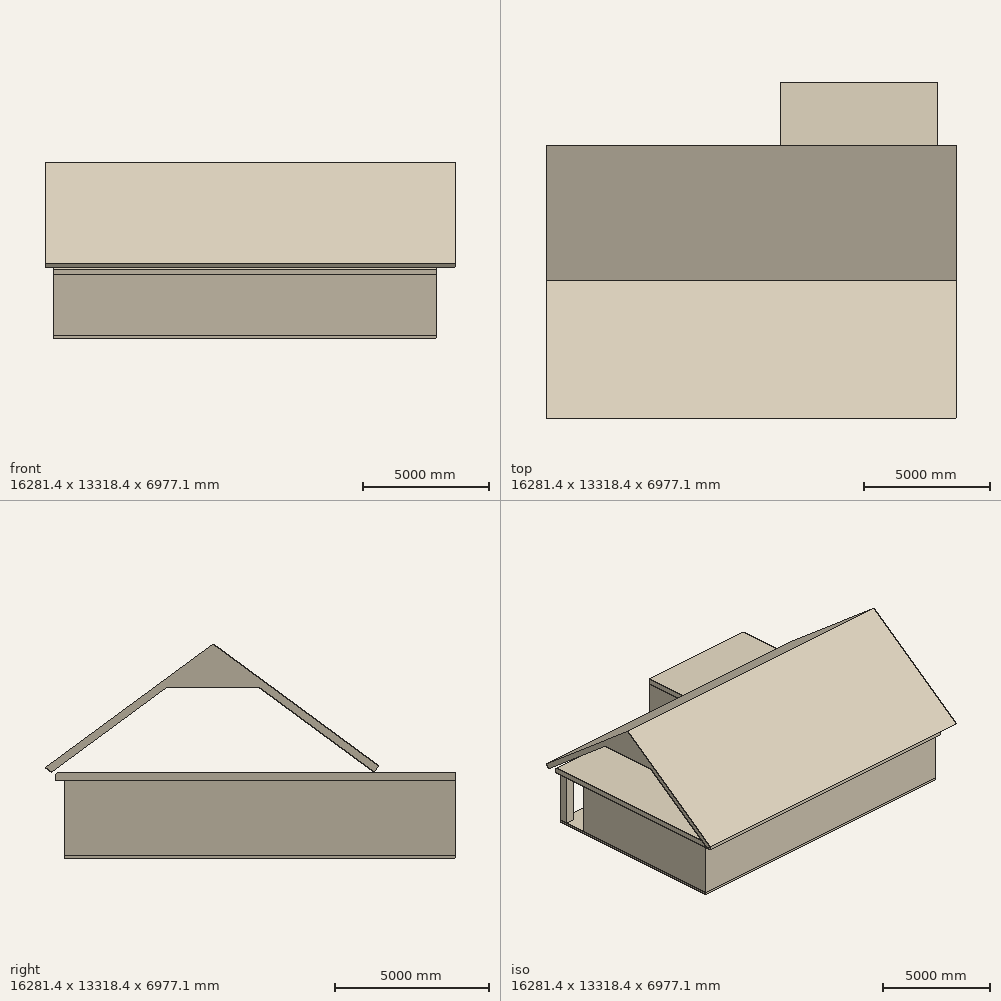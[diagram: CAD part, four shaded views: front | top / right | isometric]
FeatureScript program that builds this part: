
annotation { "Feature Type Name" : "Feature", "Feature Type Description" : "" }
export const myFeature = defineFeature(function(context is Context, id is Id, definition is map)
    precondition{}
    {
        {
            var Q0;
            Q0=qCreatedBy(makeId("Top.planeOp"),FACE);
            var sketch = newSketch(context, id + "F0", { "sketchPlane" : qUnion([Q0])});
            skLineSegment(sketch, "E0", {"start": v(0, 0) * mm, "end": v(0, 7721.6) * mm});
            skLineSegment(sketch, "E1", {"start": v(0, 7721.6) * mm, "end": v(5632.45, 7721.6) * mm});
            skLineSegment(sketch, "E2", {"start": v(5632.45, 7721.6) * mm, "end": v(5632.45, 9245.6) * mm});
            skLineSegment(sketch, "E3", {"start": v(5632.45, 9245.6) * mm, "end": v(8953.5, 9245.6) * mm});
            skLineSegment(sketch, "E4", {"start": v(8953.5, 9245.6) * mm, "end": v(8953.5, 12293.6) * mm});
            skLineSegment(sketch, "E5", {"start": v(8953.5, 12293.6) * mm, "end": v(14782.8, 12293.6) * mm});
            skLineSegment(sketch, "E6", {"start": v(14782.8, 12293.6) * mm, "end": v(14782.8, 0) * mm});
            skLineSegment(sketch, "E7", {"start": v(14782.8, 0) * mm, "end": v(0, 0) * mm});
            skLineSegment(sketch, "E8.0", {"start": v(5429.25, 7924.8) * mm, "end": v(5429.25, 9448.8) * mm});
            skLineSegment(sketch, "E8.1", {"start": v(-203.2, 7924.8) * mm, "end": v(5429.25, 7924.8) * mm});
            skLineSegment(sketch, "E8.2", {"start": v(5429.25, 9448.8) * mm, "end": v(8750.3, 9448.8) * mm});
            skLineSegment(sketch, "E8.3", {"start": v(-203.2, -203.2) * mm, "end": v(-203.2, 7924.8) * mm});
            skLineSegment(sketch, "E8.4", {"start": v(8750.3, 9448.8) * mm, "end": v(8750.3, 12496.8) * mm});
            skLineSegment(sketch, "E8.5", {"start": v(8750.3, 12496.8) * mm, "end": v(14986, 12496.8) * mm});
            skLineSegment(sketch, "E8.6", {"start": v(14986, 12496.8) * mm, "end": v(14986, -203.2) * mm});
            skLineSegment(sketch, "E8.7", {"start": v(14986, -203.2) * mm, "end": v(-203.2, -203.2) * mm});
            skLineSegment(sketch, "E9.bottom", {"start": v(-203.2, 9448.8) * mm, "end": v(254, 9448.8) * mm});
            skLineSegment(sketch, "E9.top", {"start": v(-203.2, 8991.6) * mm, "end": v(254, 8991.6) * mm});
            skLineSegment(sketch, "E9.left", {"start": v(-203.2, 9448.8) * mm, "end": v(-203.2, 8991.6) * mm});
            skLineSegment(sketch, "E9.right", {"start": v(254, 9448.8) * mm, "end": v(254, 8991.6) * mm});
            skLineSegment(sketch, "E10.bottom", {"start": v(3448.05, 9448.8) * mm, "end": v(3905.25, 9448.8) * mm});
            skLineSegment(sketch, "E10.top", {"start": v(3448.05, 8991.6) * mm, "end": v(3905.25, 8991.6) * mm});
            skLineSegment(sketch, "E10.left", {"start": v(3448.05, 9448.8) * mm, "end": v(3448.05, 8991.6) * mm});
            skLineSegment(sketch, "E10.right", {"start": v(3905.25, 9448.8) * mm, "end": v(3905.25, 8991.6) * mm});
            skSolve(sketch);
        }
        {
            var Q0;
            Q0 = qSketchRegion(id + "F0", true);
            var Q1;
            Q1=sQuery(id+"F0.wireOp",EDGE,"E8.3");
            extrude(context, id + "F1", {"entities" : qUnion([Q0]), "surfaceEntities" : qUnion([Q1]), "depth" : 2438.4 * mm});
        }
        {
            var Q0;
            Q0=qCreatedBy(makeId("Top.planeOp"),FACE);
            var sketch = newSketch(context, id + "F2", { "sketchPlane" : qUnion([Q0])});
            skLineSegment(sketch, "E11.bottom", {"start": v(3441.7, 7721.6) * mm, "end": v(3327.4, 7721.6) * mm});
            skLineSegment(sketch, "E11.top", {"start": v(3441.7, 0) * mm, "end": v(3327.4, 0) * mm});
            skLineSegment(sketch, "E11.left", {"start": v(3441.7, 7721.6) * mm, "end": v(3441.7, 0) * mm});
            skLineSegment(sketch, "E11.right", {"start": v(3327.4, 7721.6) * mm, "end": v(3327.4, 0) * mm});
            skLineSegment(sketch, "E12.bottom", {"start": v(8953.5, 9245.6) * mm, "end": v(8839.2, 9245.6) * mm});
            skLineSegment(sketch, "E12.top", {"start": v(8953.5, 4267.2) * mm, "end": v(8839.2, 4267.2) * mm});
            skLineSegment(sketch, "E12.left", {"start": v(8953.5, 9245.6) * mm, "end": v(8953.5, 4267.2) * mm});
            skLineSegment(sketch, "E12.right", {"start": v(8839.2, 9245.6) * mm, "end": v(8839.2, 4267.2) * mm});
            skLineSegment(sketch, "E13.bottom", {"start": v(8953.5, 4267.2) * mm, "end": v(14782.8, 4267.2) * mm});
            skLineSegment(sketch, "E13.top", {"start": v(8953.5, 4381.5) * mm, "end": v(14782.8, 4381.5) * mm});
            skLineSegment(sketch, "E13.left", {"start": v(8953.5, 4267.2) * mm, "end": v(8953.5, 4381.5) * mm});
            skLineSegment(sketch, "E13.right", {"start": v(14782.8, 4267.2) * mm, "end": v(14782.8, 4381.5) * mm});
            skLineSegment(sketch, "E14.bottom", {"start": v(8953.5, 5651.5) * mm, "end": v(14782.8, 5651.5) * mm});
            skLineSegment(sketch, "E14.top", {"start": v(8953.5, 5765.8) * mm, "end": v(14782.8, 5765.8) * mm});
            skLineSegment(sketch, "E14.left", {"start": v(8953.5, 5651.5) * mm, "end": v(8953.5, 5765.8) * mm});
            skLineSegment(sketch, "E14.right", {"start": v(14782.8, 5651.5) * mm, "end": v(14782.8, 5765.8) * mm});
            skLineSegment(sketch, "E15.bottom", {"start": v(12230.1, 5651.5) * mm, "end": v(12344.4, 5651.5) * mm});
            skLineSegment(sketch, "E15.top", {"start": v(12230.1, 4381.5) * mm, "end": v(12344.4, 4381.5) * mm});
            skLineSegment(sketch, "E15.left", {"start": v(12230.1, 5651.5) * mm, "end": v(12230.1, 4381.5) * mm});
            skLineSegment(sketch, "E15.right", {"start": v(12344.4, 5651.5) * mm, "end": v(12344.4, 4381.5) * mm});
            skLineSegment(sketch, "E16.bottom", {"start": v(3327.4, 3162.3) * mm, "end": v(0, 3162.3) * mm});
            skLineSegment(sketch, "E16.top", {"start": v(3327.4, 3048) * mm, "end": v(0, 3048) * mm});
            skLineSegment(sketch, "E16.left", {"start": v(3327.4, 3162.3) * mm, "end": v(3327.4, 3048) * mm});
            skLineSegment(sketch, "E16.right", {"start": v(0, 3162.3) * mm, "end": v(0, 3048) * mm});
            skLineSegment(sketch, "E17", {"start": v(0, 1638.3) * mm, "end": v(0, 1524) * mm});
            skLineSegment(sketch, "E18", {"start": v(0, 1524) * mm, "end": v(1689.1, 1524) * mm});
            skLineSegment(sketch, "E19", {"start": v(1689.1, 1524) * mm, "end": v(1689.1, 0) * mm});
            skLineSegment(sketch, "E20", {"start": v(1689.1, 0) * mm, "end": v(1803.4, 0) * mm});
            skLineSegment(sketch, "E21.0", {"start": v(1803.4, 1638.3) * mm, "end": v(1803.4, 0) * mm});
            skLineSegment(sketch, "E21.2", {"start": v(0, 1638.3) * mm, "end": v(1803.4, 1638.3) * mm});
            skLineSegment(sketch, "E22.bottom", {"start": v(4381.5, 6553.2) * mm, "end": v(4546.6, 6553.2) * mm});
            skLineSegment(sketch, "E22.top", {"start": v(4381.5, 3048) * mm, "end": v(4546.6, 3048) * mm});
            skLineSegment(sketch, "E22.left", {"start": v(4381.5, 6553.2) * mm, "end": v(4381.5, 3048) * mm});
            skLineSegment(sketch, "E22.right", {"start": v(4546.6, 6553.2) * mm, "end": v(4546.6, 3048) * mm});
            skLineSegment(sketch, "E23.bottom", {"start": v(4381.5, 3048) * mm, "end": v(3441.7, 3048) * mm});
            skLineSegment(sketch, "E23.top", {"start": v(4381.5, 3162.3) * mm, "end": v(3441.7, 3162.3) * mm});
            skLineSegment(sketch, "E23.left", {"start": v(4381.5, 3048) * mm, "end": v(4381.5, 3162.3) * mm});
            skLineSegment(sketch, "E23.right", {"start": v(3441.7, 3048) * mm, "end": v(3441.7, 3162.3) * mm});
            skLineSegment(sketch, "E24.bottom", {"start": v(4381.5, 4495.8) * mm, "end": v(3441.7, 4495.8) * mm});
            skLineSegment(sketch, "E24.top", {"start": v(4381.5, 4610.1) * mm, "end": v(3441.7, 4610.1) * mm});
            skLineSegment(sketch, "E24.left", {"start": v(4381.5, 4495.8) * mm, "end": v(4381.5, 4610.1) * mm});
            skLineSegment(sketch, "E24.right", {"start": v(3441.7, 4495.8) * mm, "end": v(3441.7, 4610.1) * mm});
            skLineSegment(sketch, "E25.bottom", {"start": v(2717.8, 723.9) * mm, "end": v(3327.4, 723.9) * mm});
            skLineSegment(sketch, "E25.top", {"start": v(2717.8, 609.6) * mm, "end": v(3327.4, 609.6) * mm});
            skLineSegment(sketch, "E25.left", {"start": v(2717.8, 723.9) * mm, "end": v(2717.8, 609.6) * mm});
            skLineSegment(sketch, "E25.right", {"start": v(3327.4, 723.9) * mm, "end": v(3327.4, 609.6) * mm});
            skLineSegment(sketch, "E26.bottom", {"start": v(1689.1, 3048) * mm, "end": v(1803.4, 3048) * mm});
            skLineSegment(sketch, "E26.top", {"start": v(1689.1, 2495.55) * mm, "end": v(1803.4, 2495.55) * mm});
            skLineSegment(sketch, "E26.left", {"start": v(1689.1, 3048) * mm, "end": v(1689.1, 2495.55) * mm});
            skLineSegment(sketch, "E26.right", {"start": v(1803.4, 3048) * mm, "end": v(1803.4, 2495.55) * mm});
            skLineSegment(sketch, "E27.bottom", {"start": v(1803.4, 1943.1) * mm, "end": v(1689.1, 1943.1) * mm});
            skLineSegment(sketch, "E27.top", {"start": v(1803.4, 1638.3) * mm, "end": v(1689.1, 1638.3) * mm});
            skLineSegment(sketch, "E27.left", {"start": v(1803.4, 1943.1) * mm, "end": v(1803.4, 1638.3) * mm});
            skLineSegment(sketch, "E27.right", {"start": v(1689.1, 1943.1) * mm, "end": v(1689.1, 1638.3) * mm});
            skLineSegment(sketch, "E28.bottom", {"start": v(1803.4, 723.9) * mm, "end": v(2108.2, 723.9) * mm});
            skLineSegment(sketch, "E28.top", {"start": v(1803.4, 609.6) * mm, "end": v(2108.2, 609.6) * mm});
            skLineSegment(sketch, "E28.left", {"start": v(1803.4, 723.9) * mm, "end": v(1803.4, 609.6) * mm});
            skLineSegment(sketch, "E28.right", {"start": v(2108.2, 723.9) * mm, "end": v(2108.2, 609.6) * mm});
            skLineSegment(sketch, "E29", {"start": v(1689.1, 2495.55) * mm, "end": v(1689.1, 1943.1) * mm, "construction": true});
            skSolve(sketch);
        }
        {
            var Q0;
            Q0 = qSketchRegion(id + "F2", true);
            extrude(context, id + "F3", {"entities" : qUnion([Q0]), "operationType" : NewBodyOperationType.ADD, "depth" : 2438.4 * mm});
        }
        {
            var Q0;
            {var subQ0=sQuery(id+"F2.wireOp",EDGE,"E11.left");Q0=makeQuery(id+"F3.opExtrude","SWEPT_FACE",FACE,{"disambiguationData":[OSD([subQ0]),TDD([makeQuery(id+"F2.imprint","IMPRINT",EDGE,{"disambiguationData":[TD([[makeQuery(id+"F2.imprint","INTERSECT",VERTEX,{"derivedFrom":[sQuery(id+"F2.wireOp",EDGE,"E11.bottom"),subQ0]}),-1.0]])],"derivedFrom":subQ0})])]});}
            var sketch = newSketch(context, id + "F4", { "sketchPlane" : qUnion([Q0])});
            skLineSegment(sketch, "E30", {"start": v(6540.5, 0) * mm, "end": v(6540.5, 195.94) * mm});
            skLineSegment(sketch, "E31", {"start": v(6540.5, 195.94) * mm, "end": v(6280.64, 195.94) * mm});
            skLineSegment(sketch, "E32", {"start": v(6280.64, 195.94) * mm, "end": v(6280.64, 391.89) * mm});
            skLineSegment(sketch, "E33", {"start": v(6280.64, 391.89) * mm, "end": v(6020.78, 391.89) * mm});
            skLineSegment(sketch, "E34", {"start": v(6020.78, 391.89) * mm, "end": v(6020.78, 587.83) * mm});
            skLineSegment(sketch, "E35", {"start": v(6020.78, 587.83) * mm, "end": v(5760.92, 587.83) * mm});
            skLineSegment(sketch, "E36", {"start": v(5760.92, 587.83) * mm, "end": v(5760.92, 783.77) * mm});
            skLineSegment(sketch, "E37", {"start": v(5760.92, 783.77) * mm, "end": v(5501.05, 783.77) * mm});
            skLineSegment(sketch, "E38", {"start": v(5501.05, 783.77) * mm, "end": v(5501.05, 979.71) * mm});
            skLineSegment(sketch, "E39", {"start": v(5501.05, 979.71) * mm, "end": v(5241.2, 979.71) * mm});
            skLineSegment(sketch, "E40", {"start": v(5241.2, 979.71) * mm, "end": v(5241.2, 1175.66) * mm});
            skLineSegment(sketch, "E41", {"start": v(5241.2, 1175.66) * mm, "end": v(4981.33, 1175.66) * mm});
            skLineSegment(sketch, "E42", {"start": v(4981.33, 1175.66) * mm, "end": v(4981.33, 1371.6) * mm});
            skLineSegment(sketch, "E43", {"start": v(4981.33, 1371.6) * mm, "end": v(4721.47, 1371.6) * mm});
            skLineSegment(sketch, "E44", {"start": v(4721.47, 1371.6) * mm, "end": v(4721.47, 1567.54) * mm});
            skLineSegment(sketch, "E45", {"start": v(4721.47, 1567.54) * mm, "end": v(4461.6, 1567.54) * mm});
            skLineSegment(sketch, "E46", {"start": v(4461.6, 1567.54) * mm, "end": v(4461.6, 1763.49) * mm});
            skLineSegment(sketch, "E47", {"start": v(4461.6, 1763.49) * mm, "end": v(4201.75, 1763.49) * mm});
            skLineSegment(sketch, "E48", {"start": v(4201.75, 1763.49) * mm, "end": v(4201.75, 1959.43) * mm});
            skLineSegment(sketch, "E49", {"start": v(4201.75, 1959.43) * mm, "end": v(3941.88, 1959.43) * mm});
            skLineSegment(sketch, "E50", {"start": v(3941.88, 1959.43) * mm, "end": v(3941.88, 2155.37) * mm});
            skLineSegment(sketch, "E51", {"start": v(3941.88, 2155.37) * mm, "end": v(3682.02, 2155.37) * mm});
            skLineSegment(sketch, "E52", {"start": v(3682.02, 2155.37) * mm, "end": v(3682.02, 2351.31) * mm});
            skLineSegment(sketch, "E53", {"start": v(3682.02, 2351.31) * mm, "end": v(3422.16, 2351.31) * mm});
            skLineSegment(sketch, "E54", {"start": v(3422.16, 2351.31) * mm, "end": v(3422.16, 2547.26) * mm});
            skLineSegment(sketch, "E55", {"start": v(3422.16, 2547.26) * mm, "end": v(3162.3, 2547.26) * mm});
            skLineSegment(sketch, "E56", {"start": v(3162.3, 2547.26) * mm, "end": v(3162.3, 2743.2) * mm, "construction": true});
            skLineSegment(sketch, "E57", {"start": v(3162.3, 2547.26) * mm, "end": v(3162.3, 2184.4) * mm});
            skLineSegment(sketch, "E58", {"start": v(3162.3, 2184.4) * mm, "end": v(3559.15, 2184.4) * mm});
            skLineSegment(sketch, "E59", {"start": v(3559.15, 2184.4) * mm, "end": v(6456.12, 0) * mm});
            skLineSegment(sketch, "E60", {"start": v(6456.12, 0) * mm, "end": v(6540.5, 0) * mm});
            skLineSegment(sketch, "E61", {"start": v(3162.3, 2547.26) * mm, "end": v(6540.5, 0) * mm, "construction": true});
            skSolve(sketch);
        }
        {
            var Q0;
            Q0=makeQuery(id+"F3.opExtrude","SWEPT_FACE",FACE,{"disambiguationData":[OSD([sQuery(id+"F2.wireOp",EDGE,"E22.right")])]});
            var sketch = newSketch(context, id + "F5", { "sketchPlane" : qUnion([Q0])});
            skLineSegment(sketch, "E62", {"start": v(4902.6, 2438.4) * mm, "end": v(6553.2, 1193.8) * mm});
            skLineSegment(sketch, "E63", {"start": v(6553.2, 1193.8) * mm, "end": v(6553.2, 2438.4) * mm});
            skLineSegment(sketch, "E64", {"start": v(6553.2, 2438.4) * mm, "end": v(4902.6, 2438.4) * mm});
            skSolve(sketch);
        }
        {
            var Q0;
            Q0 = qSketchRegion(id + "F5", true);
            extrude(context, id + "F6", {"entities" : qUnion([Q0]), "operationType" : NewBodyOperationType.REMOVE, "endBound" : BoundingType.UP_TO_NEXT, "oppositeDirection" : true, "depth" : 25.4 * mm});
        }
        {
            var Q0;
            {var subQ0=sQuery(id+"F2.wireOp",EDGE,"E11.left");Q0=makeQuery(id+"F3.opExtrude","SWEPT_FACE",FACE,{"disambiguationData":[OSD([subQ0]),TDD([makeQuery(id+"F2.imprint","IMPRINT",EDGE,{"disambiguationData":[TD([[makeQuery(id+"F2.imprint","INTERSECT",VERTEX,{"derivedFrom":[subQ0,sQuery(id+"F2.wireOp",EDGE,"E23.top"),sQuery(id+"F2.wireOp",EDGE,"E23.right")]}),1.0]])],"derivedFrom":subQ0})])]});}
            var sketch = newSketch(context, id + "F7", { "sketchPlane" : qUnion([Q0])});
            skLineSegment(sketch, "E65", {"start": v(4495.8, 2438.4) * mm, "end": v(4610.1, 2438.4) * mm});
            skLineSegment(sketch, "E66", {"start": v(4610.1, 2438.4) * mm, "end": v(4610.1, 1391.95) * mm});
            skLineSegment(sketch, "E67", {"start": v(4610.1, 1391.95) * mm, "end": v(4495.8, 1478.14) * mm});
            skLineSegment(sketch, "E68", {"start": v(4495.8, 1478.14) * mm, "end": v(4495.8, 2438.4) * mm});
            skSolve(sketch);
        }
        {
            var Q0;
            Q0 = qSketchRegion(id + "F7", true);
            var Q1;
            {var subQ0=sQuery(id+"F2.wireOp",EDGE,"E22.left");Q1=makeQuery(id+"F3.opExtrude","SWEPT_FACE",FACE,{"disambiguationData":[OSD([subQ0]),TDD([makeQuery(id+"F2.imprint","IMPRINT",EDGE,{"disambiguationData":[TD([[makeQuery(id+"F2.imprint","INTERSECT",VERTEX,{"derivedFrom":[subQ0,sQuery(id+"F2.wireOp",EDGE,"E23.top"),sQuery(id+"F2.wireOp",EDGE,"E23.left")]}),1.0]])],"derivedFrom":subQ0})])]});}
            extrude(context, id + "F8", {"entities" : qUnion([Q0]), "operationType" : NewBodyOperationType.REMOVE, "endBound" : BoundingType.UP_TO_SURFACE, "endBoundEntityFace" : qUnion([Q1]), "depth" : 25.4 * mm});
        }
        {
            var Q0;
            Q0 = qSketchRegion(id + "F4", true);
            var Q1;
            {var subQ0=sQuery(id+"F2.wireOp",EDGE,"E22.left");Q1=makeQuery(id+"F3.opExtrude","SWEPT_FACE",FACE,{"disambiguationData":[OSD([subQ0]),TDD([makeQuery(id+"F2.imprint","IMPRINT",EDGE,{"disambiguationData":[TD([[makeQuery(id+"F2.imprint","INTERSECT",VERTEX,{"derivedFrom":[subQ0,sQuery(id+"F2.wireOp",EDGE,"E23.top"),sQuery(id+"F2.wireOp",EDGE,"E23.left")]}),1.0]])],"derivedFrom":subQ0})])]});}
            var Q2;
            {var subQ0=sQuery(id+"F2.wireOp",EDGE,"E22.left");Q2=makeQuery(id+"F3.opExtrude","SWEPT_FACE",FACE,{"disambiguationData":[OSD([subQ0]),TDD([makeQuery(id+"F2.imprint","IMPRINT",EDGE,{"disambiguationData":[TD([[makeQuery(id+"F2.imprint","INTERSECT",VERTEX,{"derivedFrom":[subQ0,sQuery(id+"F2.wireOp",EDGE,"E23.top"),sQuery(id+"F2.wireOp",EDGE,"E23.left")]}),1.0]])],"derivedFrom":subQ0})])]});}
            extrude(context, id + "F9", {"entities" : qUnion([Q0]), "operationType" : NewBodyOperationType.ADD, "endBound" : BoundingType.UP_TO_SURFACE, "endBoundEntityFace" : qUnion([Q1]), "depth" : 660.4 * mm});
        }
        {
            var Q0;
            {var subQ0=sQuery(id+"F2.wireOp",EDGE,"E23.top");var subQ20=sQuery(id+"F2.wireOp",EDGE,"E11.left");var subQ22=sQuery(id+"F2.wireOp",EDGE,"E11.bottom");var subQ23=sQuery(id+"F0.wireOp",EDGE,"E1");Q0=makeQuery(id+"F9.boolean.opBoolean","SPLIT",FACE,{"disambiguationData":[TD([makeQuery(id+"F1.opExtrude","SWEPT_FACE",FACE,{"disambiguationData":[OSD([subQ23])]})])],"derivedFrom":makeQuery(id+"F8.boolean.opBoolean","MERGE",FACE,{"derivedFrom":[makeQuery(id+"F3.opExtrude","SWEPT_FACE",FACE,{"disambiguationData":[OSD([subQ20]),TDD([makeQuery(id+"F2.imprint","IMPRINT",EDGE,{"disambiguationData":[TD([[makeQuery(id+"F2.imprint","INTERSECT",VERTEX,{"derivedFrom":[subQ22,subQ20]}),-1.0]])],"derivedFrom":subQ20})])]}),makeQuery(id+"F3.opExtrude","SWEPT_FACE",FACE,{"disambiguationData":[OSD([subQ20]),TDD([makeQuery(id+"F2.imprint","IMPRINT",EDGE,{"disambiguationData":[TD([[makeQuery(id+"F2.imprint","INTERSECT",VERTEX,{"derivedFrom":[subQ20,subQ0,sQuery(id+"F2.wireOp",EDGE,"E23.right")]}),1.0]])],"derivedFrom":subQ20})])]}),makeQuery(id+"F8.opExtrude","CAP_FACE",FACE,{"disambiguationData":[OSD([sQuery(id+"F7.wireOp",EDGE,"E65"),sQuery(id+"F7.wireOp",EDGE,"E66"),sQuery(id+"F7.wireOp",EDGE,"E67"),sQuery(id+"F7.wireOp",EDGE,"E68")])],"isStart":true})]})});}
            var sketch = newSketch(context, id + "F10", { "sketchPlane" : qUnion([Q0])});
            skLineSegment(sketch, "E69.bottom", {"start": v(6724.65, 0) * mm, "end": v(7537.45, 0) * mm});
            skLineSegment(sketch, "E69.top", {"start": v(6724.65, 2032) * mm, "end": v(7537.45, 2032) * mm});
            skLineSegment(sketch, "E69.left", {"start": v(6724.65, 0) * mm, "end": v(6724.65, 2032) * mm});
            skLineSegment(sketch, "E69.right", {"start": v(7537.45, 0) * mm, "end": v(7537.45, 2032) * mm});
            skLineSegment(sketch, "E70", {"start": v(6724.65, 0) * mm, "end": v(6540.5, 0) * mm, "construction": true});
            skLineSegment(sketch, "E71", {"start": v(7537.45, 0) * mm, "end": v(7721.6, 0) * mm});
            skSolve(sketch);
        }
        {
            var Q0;
            Q0 = qSketchRegion(id + "F10", true);
            extrude(context, id + "F11", {"entities" : qUnion([Q0]), "operationType" : NewBodyOperationType.REMOVE, "endBound" : BoundingType.UP_TO_NEXT, "oppositeDirection" : true, "depth" : 25.4 * mm});
        }
        {
            var Q0;
            Q0=makeQuery(id+"F3.opExtrude","SWEPT_FACE",FACE,{"disambiguationData":[OSD([sQuery(id+"F2.wireOp",EDGE,"E19")])]});
            var sketch = newSketch(context, id + "F12", { "sketchPlane" : qUnion([Q0])});
            skLineSegment(sketch, "E72.bottom", {"start": v(-1422.4, 0) * mm, "end": v(-812.8, 0) * mm});
            skLineSegment(sketch, "E72.top", {"start": v(-1422.4, 2032) * mm, "end": v(-812.8, 2032) * mm});
            skLineSegment(sketch, "E72.left", {"start": v(-1422.4, 0) * mm, "end": v(-1422.4, 2032) * mm});
            skLineSegment(sketch, "E72.right", {"start": v(-812.8, 0) * mm, "end": v(-812.8, 2032) * mm});
            skSolve(sketch);
        }
        {
            var Q0;
            Q0 = qSketchRegion(id + "F12", true);
            extrude(context, id + "F13", {"entities" : qUnion([Q0]), "operationType" : NewBodyOperationType.REMOVE, "endBound" : BoundingType.UP_TO_NEXT, "oppositeDirection" : true, "depth" : 25.4 * mm});
        }
        {
            var Q0;
            Q0=makeQuery(id+"F3.opExtrude","SWEPT_FACE",FACE,{"disambiguationData":[OSD([sQuery(id+"F2.wireOp",EDGE,"E16.top")])]});
            var sketch = newSketch(context, id + "F14", { "sketchPlane" : qUnion([Q0])});
            skLineSegment(sketch, "E73.bottom", {"start": v(1955.8, 0) * mm, "end": v(2565.4, 0) * mm});
            skLineSegment(sketch, "E73.top", {"start": v(1955.8, 2032) * mm, "end": v(2565.4, 2032) * mm});
            skLineSegment(sketch, "E73.left", {"start": v(1955.8, 0) * mm, "end": v(1955.8, 2032) * mm});
            skLineSegment(sketch, "E73.right", {"start": v(2565.4, 0) * mm, "end": v(2565.4, 2032) * mm});
            skSolve(sketch);
        }
        {
            var Q0;
            Q0 = qSketchRegion(id + "F14", true);
            extrude(context, id + "F15", {"entities" : qUnion([Q0]), "operationType" : NewBodyOperationType.REMOVE, "endBound" : BoundingType.UP_TO_NEXT, "oppositeDirection" : true, "depth" : 25.4 * mm});
        }
        {
            var Q0;
            Q0=qCreatedBy(makeId("Top.planeOp"),FACE);
            var sketch = newSketch(context, id + "F16", { "sketchPlane" : qUnion([Q0])});
            skLineSegment(sketch, "E74.bottom", {"start": v(1689.1, 2438.4) * mm, "end": v(304.8, 2438.4) * mm});
            skLineSegment(sketch, "E74.top", {"start": v(1689.1, 3048) * mm, "end": v(304.8, 3048) * mm});
            skLineSegment(sketch, "E74.left", {"start": v(1689.1, 2438.4) * mm, "end": v(1689.1, 3048) * mm});
            skLineSegment(sketch, "E74.right", {"start": v(304.8, 2438.4) * mm, "end": v(304.8, 3048) * mm});
            skLineSegment(sketch, "E75.bottom", {"start": v(1689.1, 1943.1) * mm, "end": v(304.8, 1943.1) * mm});
            skLineSegment(sketch, "E75.top", {"start": v(1689.1, 1638.3) * mm, "end": v(304.8, 1638.3) * mm});
            skLineSegment(sketch, "E75.left", {"start": v(1689.1, 1943.1) * mm, "end": v(1689.1, 1638.3) * mm});
            skLineSegment(sketch, "E75.right", {"start": v(304.8, 1943.1) * mm, "end": v(304.8, 1638.3) * mm});
            skLineSegment(sketch, "E76.bottom", {"start": v(304.8, 3048) * mm, "end": v(0, 3048) * mm});
            skLineSegment(sketch, "E76.top", {"start": v(304.8, 1638.3) * mm, "end": v(0, 1638.3) * mm});
            skLineSegment(sketch, "E76.left", {"start": v(304.8, 3048) * mm, "end": v(304.8, 1638.3) * mm});
            skLineSegment(sketch, "E76.right", {"start": v(0, 3048) * mm, "end": v(0, 1638.3) * mm});
            skLineSegment(sketch, "E77.bottom", {"start": v(1803.4, 609.6) * mm, "end": v(2108.2, 609.6) * mm});
            skLineSegment(sketch, "E77.top", {"start": v(1803.4, 0) * mm, "end": v(2108.2, 0) * mm});
            skLineSegment(sketch, "E77.left", {"start": v(1803.4, 609.6) * mm, "end": v(1803.4, 0) * mm});
            skLineSegment(sketch, "E77.right", {"start": v(2108.2, 609.6) * mm, "end": v(2108.2, 0) * mm});
            skLineSegment(sketch, "E78.bottom", {"start": v(2717.8, 609.6) * mm, "end": v(3327.4, 609.6) * mm});
            skLineSegment(sketch, "E78.top", {"start": v(2717.8, 0) * mm, "end": v(3327.4, 0) * mm});
            skLineSegment(sketch, "E78.left", {"start": v(2717.8, 609.6) * mm, "end": v(2717.8, 0) * mm});
            skLineSegment(sketch, "E78.right", {"start": v(3327.4, 609.6) * mm, "end": v(3327.4, 0) * mm});
            skSolve(sketch);
        }
        {
            var Q0;
            Q0 = qSketchRegion(id + "F16", true);
            extrude(context, id + "F17", {"entities" : qUnion([Q0]), "operationType" : NewBodyOperationType.ADD, "depth" : 2133.6 * mm});
        }
        {
            var Q0;
            Q0=qCreatedBy(makeId("Top.planeOp"),FACE);
            var sketch = newSketch(context, id + "F18", { "sketchPlane" : qUnion([Q0])});
            skLineSegment(sketch, "E79.bottom", {"start": v(2717.8, 3048) * mm, "end": v(3327.4, 3048) * mm});
            skLineSegment(sketch, "E79.top", {"start": v(2717.8, 723.9) * mm, "end": v(3327.4, 723.9) * mm});
            skLineSegment(sketch, "E79.left", {"start": v(2717.8, 3048) * mm, "end": v(2717.8, 723.9) * mm});
            skLineSegment(sketch, "E79.right", {"start": v(3327.4, 3048) * mm, "end": v(3327.4, 723.9) * mm});
            skEllipse(sketch, "E80", {"center": v(3022.6, 2736.85) * mm, "majorRadius": 254 * mm, "minorRadius": 190.5 * mm, "majorAxis": v(0, -1)});
            skEllipse(sketch, "E81", {"center": v(3022.6, 1035.05) * mm, "majorRadius": 254 * mm, "minorRadius": 190.5 * mm, "majorAxis": v(0, -1)});
            skLineSegment(sketch, "E82", {"start": v(2832.1, 1035.05) * mm, "end": v(3213.1, 1035.05) * mm, "construction": true});
            skLineSegment(sketch, "E83", {"start": v(3022.6, 781.05) * mm, "end": v(3022.6, 1289.05) * mm, "construction": true});
            skLineSegment(sketch, "E84", {"start": v(3022.6, 1289.05) * mm, "end": v(3022.6, 2482.85) * mm, "construction": true});
            skLineSegment(sketch, "E85", {"start": v(3022.6, 2482.85) * mm, "end": v(3022.6, 2990.85) * mm, "construction": true});
            skLineSegment(sketch, "E86", {"start": v(3213.1, 2736.85) * mm, "end": v(2832.1, 2736.85) * mm, "construction": true});
            skLineSegment(sketch, "E87", {"start": v(2832.1, 1035.05) * mm, "end": v(2717.8, 1035.05) * mm, "construction": true});
            skLineSegment(sketch, "E88", {"start": v(3213.1, 1035.05) * mm, "end": v(3327.4, 1035.05) * mm, "construction": true});
            skLineSegment(sketch, "E89", {"start": v(3022.6, 781.05) * mm, "end": v(3022.6, 723.9) * mm, "construction": true});
            skLineSegment(sketch, "E90", {"start": v(2832.1, 2736.85) * mm, "end": v(2717.8, 2736.85) * mm, "construction": true});
            skLineSegment(sketch, "E91", {"start": v(3213.1, 2736.85) * mm, "end": v(3327.4, 2736.85) * mm, "construction": true});
            skLineSegment(sketch, "E92", {"start": v(3022.6, 2990.85) * mm, "end": v(3022.6, 3048) * mm, "construction": true});
            skSolve(sketch);
        }
        {
            var Q0;
            Q0 = qSketchRegion(id + "F18", true);
            extrude(context, id + "F19", {"entities" : qUnion([Q0]), "operationType" : NewBodyOperationType.ADD, "depth" : 787.4 * mm});
        }
        {
            var Q0;
            Q0=qCreatedBy(makeId("Top.planeOp"),FACE);
            var sketch = newSketch(context, id + "F20", { "sketchPlane" : qUnion([Q0])});
            skLineSegment(sketch, "E93.bottom", {"start": v(1384.3, 1943.1) * mm, "end": v(1689.1, 1943.1) * mm});
            skLineSegment(sketch, "E93.top", {"start": v(1384.3, 1638.3) * mm, "end": v(1689.1, 1638.3) * mm});
            skLineSegment(sketch, "E93.left", {"start": v(1384.3, 1943.1) * mm, "end": v(1384.3, 1638.3) * mm});
            skLineSegment(sketch, "E93.right", {"start": v(1689.1, 1943.1) * mm, "end": v(1689.1, 1638.3) * mm});
            skSolve(sketch);
        }
        {
            var Q0;
            Q0 = qSketchRegion(id + "F20", true);
            extrude(context, id + "F21", {"entities" : qUnion([Q0]), "operationType" : NewBodyOperationType.ADD, "depth" : 2438.4 * mm});
        }
        {
            var Q0;
            Q0=makeQuery(id+"F19.boolean.opBoolean","MERGE",FACE,{"derivedFrom":[makeQuery(id+"F3.opExtrude","SWEPT_FACE",FACE,{"disambiguationData":[OSD([sQuery(id+"F2.wireOp",EDGE,"E25.left")])]}),makeQuery(id+"F19.opExtrude","SWEPT_FACE",FACE,{"disambiguationData":[OSD([sQuery(id+"F18.wireOp",EDGE,"E79.left")])]})]});
            var sketch = newSketch(context, id + "F22", { "sketchPlane" : qUnion([Q0])});
            skLineSegment(sketch, "E94.bottom", {"start": v(-2266.95, 660.4) * mm, "end": v(-1504.95, 660.4) * mm});
            skLineSegment(sketch, "E94.top", {"start": v(-2266.95, 0) * mm, "end": v(-1504.95, 0) * mm});
            skLineSegment(sketch, "E94.left", {"start": v(-2266.95, 660.4) * mm, "end": v(-2266.95, 0) * mm});
            skLineSegment(sketch, "E94.right", {"start": v(-1504.95, 660.4) * mm, "end": v(-1504.95, 0) * mm});
            skLineSegment(sketch, "E95", {"start": v(-3048, 0) * mm, "end": v(-2266.95, 0) * mm, "construction": true});
            skLineSegment(sketch, "E96", {"start": v(-723.9, 0) * mm, "end": v(-1504.95, 0) * mm, "construction": true});
            skLineSegment(sketch, "E97", {"start": v(-723.9, 0) * mm, "end": v(-723.9, 787.4) * mm, "construction": true});
            skSolve(sketch);
        }
        {
            var Q0;
            Q0 = qSketchRegion(id + "F22", true);
            extrude(context, id + "F23", {"entities" : qUnion([Q0]), "operationType" : NewBodyOperationType.REMOVE, "oppositeDirection" : true, "depth" : 609.6 * mm});
        }
        {
            var Q0;
            Q0=makeQuery(id+"F19.opExtrude","CAP_FACE",FACE,{"disambiguationData":[OSD([sQuery(id+"F18.wireOp",EDGE,"E79.bottom"),sQuery(id+"F18.wireOp",EDGE,"E79.top"),sQuery(id+"F18.wireOp",EDGE,"E79.left"),sQuery(id+"F18.wireOp",EDGE,"E79.right"),sQuery(id+"F18.wireOp",EDGE,"E80"),sQuery(id+"F18.wireOp",EDGE,"E81")])],"isStart":false});
            var sketch = newSketch(context, id + "F24", { "sketchPlane" : qUnion([Q0])});
            skLineSegment(sketch, "E98.bottom", {"start": v(2743.2, 1358.9) * mm, "end": v(3327.4, 1358.9) * mm});
            skLineSegment(sketch, "E98.top", {"start": v(2743.2, 1352.55) * mm, "end": v(3327.4, 1352.55) * mm});
            skLineSegment(sketch, "E98.left", {"start": v(2743.2, 1358.9) * mm, "end": v(2743.2, 1352.55) * mm});
            skLineSegment(sketch, "E98.right", {"start": v(3327.4, 1358.9) * mm, "end": v(3327.4, 1352.55) * mm});
            skLineSegment(sketch, "E99", {"start": v(3022.6, 1289.05) * mm, "end": v(3022.6, 1352.55) * mm, "construction": true});
            skLineSegment(sketch, "E100", {"start": v(3022.6, 2413) * mm, "end": v(3022.6, 1358.9) * mm, "construction": true});
            skLineSegment(sketch, "E101.bottom", {"start": v(2743.2, 2419.35) * mm, "end": v(3327.4, 2419.35) * mm});
            skLineSegment(sketch, "E101.top", {"start": v(2743.2, 2413) * mm, "end": v(3327.4, 2413) * mm});
            skLineSegment(sketch, "E101.left", {"start": v(2743.2, 2419.35) * mm, "end": v(2743.2, 2413) * mm});
            skLineSegment(sketch, "E101.right", {"start": v(3327.4, 2419.35) * mm, "end": v(3327.4, 2413) * mm});
            skLineSegment(sketch, "E102", {"start": v(3022.6, 2419.35) * mm, "end": v(3022.6, 2482.85) * mm, "construction": true});
            skSolve(sketch);
        }
        {
            var Q0;
            Q0 = qSketchRegion(id + "F24", true);
            extrude(context, id + "F25", {"entities" : qUnion([Q0]), "operationType" : NewBodyOperationType.ADD, "depth" : 1651 * mm});
        }
        {
            var Q0;
            Q0=qCreatedBy(makeId("Top.planeOp"),FACE);
            var sketch = newSketch(context, id + "F26", { "sketchPlane" : qUnion([Q0])});
            skLineSegment(sketch, "E103.bottom", {"start": v(1733.55, 1968.5) * mm, "end": v(1765.3, 1968.5) * mm});
            skLineSegment(sketch, "E103.top", {"start": v(1733.55, 2495.55) * mm, "end": v(1765.3, 2495.55) * mm});
            skLineSegment(sketch, "E103.left", {"start": v(1733.55, 1968.5) * mm, "end": v(1733.55, 2495.55) * mm});
            skLineSegment(sketch, "E103.right", {"start": v(1765.3, 1968.5) * mm, "end": v(1765.3, 2495.55) * mm});
            skLineSegment(sketch, "E104.bottom", {"start": v(2133.6, 685.8) * mm, "end": v(2717.8, 685.8) * mm});
            skLineSegment(sketch, "E104.top", {"start": v(2133.6, 654.05) * mm, "end": v(2717.8, 654.05) * mm});
            skLineSegment(sketch, "E104.left", {"start": v(2133.6, 685.8) * mm, "end": v(2133.6, 654.05) * mm});
            skLineSegment(sketch, "E104.right", {"start": v(2717.8, 685.8) * mm, "end": v(2717.8, 654.05) * mm});
            skSolve(sketch);
        }
        {
            var Q0;
            Q0 = qSketchRegion(id + "F26", true);
            extrude(context, id + "F27", {"entities" : qUnion([Q0]), "operationType" : NewBodyOperationType.ADD, "depth" : 2438.4 * mm});
        }
        {
            var Q0;
            Q0=qCreatedBy(makeId("Top.planeOp"),FACE);
            var sketch = newSketch(context, id + "F28", { "sketchPlane" : qUnion([Q0])});
            skLineSegment(sketch, "E105.bottom", {"start": v(0, 0) * mm, "end": v(749.3, 0) * mm});
            skLineSegment(sketch, "E105.top", {"start": v(0, 1524) * mm, "end": v(749.3, 1524) * mm});
            skLineSegment(sketch, "E105.left", {"start": v(0, 0) * mm, "end": v(0, 1524) * mm});
            skLineSegment(sketch, "E105.right", {"start": v(749.3, 0) * mm, "end": v(749.3, 1524) * mm});
            skSolve(sketch);
        }
        {
            var Q0;
            Q0 = qSketchRegion(id + "F28", true);
            extrude(context, id + "F29", {"entities" : qUnion([Q0]), "operationType" : NewBodyOperationType.ADD, "depth" : 355.6 * mm});
        }
        {
            var Q0;
            Q0=qCreatedBy(makeId("Top.planeOp"),FACE);
            var sketch = newSketch(context, id + "F30", { "sketchPlane" : qUnion([Q0])});
            skLineSegment(sketch, "E106.bottom", {"start": v(1524, 0) * mm, "end": v(1066.8, 0) * mm});
            skLineSegment(sketch, "E106.left", {"start": v(1524, 0) * mm, "end": v(1524, 152.4) * mm});
            skLineSegment(sketch, "E106.right", {"start": v(1066.8, 0) * mm, "end": v(1066.8, 152.4) * mm});
            skFitSpline(sketch, "E107", {"points": [v(1168.4, 152.4) * mm, v(1117.6, 444.5) * mm, v(1295.4, 698.5) * mm, v(1473.2, 444.5) * mm, v(1422.4, 152.4) * mm], "startDerivative": vector(0, 616.5) * mm, "endDerivative": vector(0, -616.5) * mm});
            skLineSegment(sketch, "E108", {"start": v(1066.8, 152.4) * mm, "end": v(1168.4, 152.4) * mm});
            skLineSegment(sketch, "E109", {"start": v(1422.4, 152.4) * mm, "end": v(1524, 152.4) * mm});
            skLineSegment(sketch, "E110", {"start": v(1168.4, 152.4) * mm, "end": v(1422.4, 152.4) * mm});
            skLineSegment(sketch, "E111", {"start": v(1295.4, 698.5) * mm, "end": v(1295.4, 152.4) * mm, "construction": true});
            skPoint(sketch, "E111.endSnap0", {"position": v(1295.4, 152.4) * mm});
            skLineSegment(sketch, "E112", {"start": v(1117.6, 444.5) * mm, "end": v(1295.4, 444.5) * mm, "construction": true});
            skLineSegment(sketch, "E113", {"start": v(1295.4, 444.5) * mm, "end": v(1473.2, 444.5) * mm, "construction": true});
            skSolve(sketch);
        }
        {
            var Q0;
            Q0=makeQuery(id+"F30.imprint","IMPRINT",FACE,{"disambiguationData":[TD([[makeQuery(id+"F30.imprint","IMPRINT",EDGE,{"derivedFrom":sQuery(id+"F30.wireOp",EDGE,"E106.bottom")}),-1.0]])]});
            extrude(context, id + "F31", {"entities" : qUnion([Q0]), "operationType" : NewBodyOperationType.ADD, "depth" : 609.6 * mm});
        }
        {
            var Q0;
            Q0=makeQuery(id+"F30.imprint","IMPRINT",FACE,{"disambiguationData":[TD([[makeQuery(id+"F30.imprint","IMPRINT",EDGE,{"derivedFrom":sQuery(id+"F30.wireOp",EDGE,"E107")}),-1.0]])]});
            extrude(context, id + "F32", {"entities" : qUnion([Q0]), "operationType" : NewBodyOperationType.ADD, "depth" : 355.6 * mm});
        }
        {
            var Q0;
            Q0=qCreatedBy(makeId("Top.planeOp"),FACE);
            cPlane(context, id + "F33", {"entities" : qUnion([Q0]), "cplaneType" : CPlaneType.OFFSET, "offset" : 104.77 * mm, "oppositeDirection" : true, "width" : 152.4 * mm, "height" : 152.4 * mm});
        }
        {
            var Q0;
            Q0=qCreatedBy(id+"F33.planeOp",FACE);
            var sketch = newSketch(context, id + "F34", { "sketchPlane" : qUnion([Q0])});
            skLineSegment(sketch, "E114", {"start": v(-203.2, -203.2) * mm, "end": v(-203.2, 9448.8) * mm});
            skLineSegment(sketch, "E115", {"start": v(-203.2, 9448.8) * mm, "end": v(8750.3, 9448.8) * mm});
            skLineSegment(sketch, "E116", {"start": v(8750.3, 9448.8) * mm, "end": v(8750.3, 12496.8) * mm});
            skLineSegment(sketch, "E117", {"start": v(8750.3, 12496.8) * mm, "end": v(14986, 12496.8) * mm});
            skLineSegment(sketch, "E118", {"start": v(14986, 12496.8) * mm, "end": v(14986, -203.2) * mm});
            skLineSegment(sketch, "E119", {"start": v(14986, -203.2) * mm, "end": v(-203.2, -203.2) * mm});
            skSolve(sketch);
        }
        {
            var Q0;
            Q0 = qSketchRegion(id + "F34", true);
            extrude(context, id + "F35", {"entities" : qUnion([Q0]), "operationType" : NewBodyOperationType.ADD, "depth" : 101.6 * mm});
        }
        {
            var Q0;
            Q0=qCreatedBy(makeId("Top.planeOp"),FACE);
            cPlane(context, id + "F36", {"entities" : qUnion([Q0]), "cplaneType" : CPlaneType.OFFSET, "offset" : 2441.57 * mm, "width" : 152.4 * mm, "height" : 152.4 * mm});
        }
        {
            var Q0;
            Q0=qCreatedBy(id+"F36.planeOp",FACE);
            var sketch = newSketch(context, id + "F37", { "sketchPlane" : qUnion([Q0])});
            skLineSegment(sketch, "E120", {"start": v(-203.2, -508) * mm, "end": v(-203.2, 9753.6) * mm});
            skLineSegment(sketch, "E121", {"start": v(-203.2, 9753.6) * mm, "end": v(8750.3, 9753.6) * mm});
            skLineSegment(sketch, "E122", {"start": v(8750.3, 9753.6) * mm, "end": v(8750.3, 12496.8) * mm});
            skLineSegment(sketch, "E123", {"start": v(8750.3, 12496.8) * mm, "end": v(14986, 12496.8) * mm});
            skLineSegment(sketch, "E124", {"start": v(14986, 12496.8) * mm, "end": v(14986, -508) * mm});
            skLineSegment(sketch, "E125", {"start": v(14986, -508) * mm, "end": v(-203.2, -508) * mm});
            skLineSegment(sketch, "E126.bottom", {"start": v(3441.7, 6540.5) * mm, "end": v(4381.5, 6540.5) * mm});
            skLineSegment(sketch, "E126.top", {"start": v(3441.7, 3162.3) * mm, "end": v(4381.5, 3162.3) * mm});
            skLineSegment(sketch, "E126.left", {"start": v(3441.7, 6540.5) * mm, "end": v(3441.7, 3162.3) * mm});
            skLineSegment(sketch, "E126.right", {"start": v(4381.5, 6540.5) * mm, "end": v(4381.5, 3162.3) * mm});
            skLineSegment(sketch, "E127", {"start": v(8750.3, 9753.6) * mm, "end": v(8750.3, 9448.8) * mm, "construction": true});
            skLineSegment(sketch, "E128", {"start": v(-203.2, -508) * mm, "end": v(-203.2, -203.2) * mm});
            skSolve(sketch);
        }
        {
            var Q0;
            Q0 = qSketchRegion(id + "F37", true);
            extrude(context, id + "F38", {"entities" : qUnion([Q0]), "depth" : 260.35 * mm});
        }
        {
            var Q0;
            Q0=makeQuery(id+"F38.opExtrude","CAP_EDGE",EDGE,{"disambiguationData":[OSD([sQuery(id+"F37.wireOp",EDGE,"E121")])],"isStart":false});
            var Q1;
            Q1=makeQuery(id+"F38.opExtrude","CAP_EDGE",EDGE,{"disambiguationData":[OSD([sQuery(id+"F37.wireOp",EDGE,"E125")])],"isStart":false});
            chamfer(context, id + "F39", {"entities" : qUnion([Q0, Q1]), "chamferType" : ChamferType.OFFSET_ANGLE, "width" : 101.6 * mm, "oppositeDirection" : true, "angle" : 36.37 * degree, "tangentPropagation" : true});
        }
        {
            var Q0;
            Q0=qCreatedBy(makeId("Right.planeOp"),FACE);
            var sketch = newSketch(context, id + "F40", { "sketchPlane" : qUnion([Q0])});
            skLineSegment(sketch, "E129", {"start": v(10013.3, 2909.62) * mm, "end": v(4632.44, 6872.38) * mm});
            skLineSegment(sketch, "E130", {"start": v(4632.44, 6872.38) * mm, "end": v(-821.6, 2855.72) * mm});
            skLineSegment(sketch, "E131", {"start": v(10013.3, 2909.62) * mm, "end": v(9862.67, 2705.1) * mm});
            skLineSegment(sketch, "E132", {"start": v(9862.67, 2705.1) * mm, "end": v(6137.8, 5448.3) * mm});
            skLineSegment(sketch, "E133", {"start": v(3107.8, 5448.3) * mm, "end": v(-617.07, 2705.1) * mm});
            skLineSegment(sketch, "E134", {"start": v(-617.07, 2705.1) * mm, "end": v(-821.6, 2855.72) * mm});
            skLineSegment(sketch, "E135", {"start": v(6137.8, 5448.3) * mm, "end": v(3107.8, 5448.3) * mm});
            skLineSegment(sketch, "E136", {"start": v(-617.07, 2705.1) * mm, "end": v(9862.67, 2705.1) * mm, "construction": true});
            skLineSegment(sketch, "E137", {"start": v(9448.8, 3009.9) * mm, "end": v(-203.2, 3009.9) * mm, "construction": true});
            skSolve(sketch);
        }
        {
            var Q0;
            Q0 = qSketchRegion(id + "F40", true);
            extrude(context, id + "F41", {"entities" : qUnion([Q0]), "depth" : 15748 * mm, "hasSecondDirection" : true, "secondDirectionOppositeDirection" : true, "secondDirectionDepth" : 533.4 * mm});
        }
    });
